# Revit family: PRD_FrankeWS_PprTwlDspnsrs_EXOSPaperTowelDispenser_EXOS637X_637B_637W
name_source: partatom
category: Specialty Equipment
revit_build: Autodesk Revit 2018 (Build: 20190510_1515(x64)
units: mm (PartAtom-declared; Revit-internal decimal feet)

## family parameters
Cut with Voids When Loaded = No
Host = Face
OmniClass Number = 23.40.20.21.17
OmniClass Title = Paper Towel Dispensers, Disposal Units
Part Type = Normal
Room Calculation Point = No
Round Connector Dimension = Use Diameter
Shared = No

## types (3) — shared parameters
AssetType = Fixed
Category = Pr_40_70_22_62, Paper Towel Dispensers
Default Elevation = 1200 mm
DispenserMaterial = PRD_AR_StainlessSteel_SatinFinished
DurationUnit = year
Features = stainless steel, surface satin finished
FillingQuantity = 1
FillingQuantityUom = Rolls
Finish = satin finished
IfcExportAs = IfcFurnitureType
IfcExportType = USERDEFINED
IntegralAccessories = incl. mounting materials
IsBuiltIn = TRUE
Lock = Key-lock
MainColor = stainless steel
Manufacturer = KWC Group AG
ManufacturerName = KWC Group AG
ManufacturerURL = www.kwc.com
Material = stainless steel
MaterialCode = 1.4301
MaterialThickness = 1.20 mm
MaximumDepthDiameterOfConsumable = 200.00 mm
MaximumWidthOfConsumable = 205.00 mm
NBSDescription = Paper towel dispensers
NBSReference = 45-35-72/344
NominalDepth = 210 mm  [stored 0.688976 ft]
NominalHeight = 425 mm  [stored 1.39436 ft]
NominalWidth = 300 mm  [stored 0.984252 ft]
ProductInformation = https://pim.kwc.com
Size = 300 x 425 x 210 mm
Style = Dispenser
SurfaceTreatment = InoxPlus (anti fingerprint)
TypeOfConsumable = Paper roll
TypeOfFixing = Screw
TypeOfMounting = Wall mounting
TypeOfOperation = Manual operation
URL = www.kwc.com
Uniclass2015Code = Pr_40_70_22_62
Uniclass2015Title = Paper towel dispensers
Uniclass2015Version = Products v1.17
Version = 1
WarrantyDurationUnit = year

## per-type parameters (varying)
| type | AdditionalPanel | BIMObjectName | Description | GrossWeight | ModelNumber | Name | NetWeight | PanelMaterial |
| EXOS637X | No | PRD_AR_PaperTowelDispensers_EXOSPaperTowelDispenser_EXOS637X | Manual paper towel dispenser for wall mounting, stainless steel with satin finish, front and casing with InoxPlus surface refinement for the reduction of finger marks and better cleaning characteristics (easy to clean), material thickness 1.2 mm, maximum roll width 205 mm, maximum roll diameter 200 mm, paper perforation length 260 mm, adjustable paper roll holder for optimised paper dispensing, includes mounting materials. | 9.64 kg | 2030022950 | Paper Towel Dispenser EXOS637X | 8.24 kg | PRD_AR_StainlessSteel_SatinFinished |
| EXOS637B | Yes | PRD_AR_PaperTowelDispensers_EXOSPaperTowelDispenser_EXOS637B | Manual paper towel dispenser for wall mounting, stainless steel with satin finish, black safety glass front panel, casing with InoxPlus surface refinement for the reduction of finger marks and better cleaning characteristics (easy to clean), material thickness 1.2 mm, maximum roll width 205 mm, maximum roll diameter 200 mm, paper perforation length 260 mm, adjustable paper roll holder for optimised paper dispensing, includes mounting materials. | 10.80 kg | 2030022951 | Paper Towel Dispenser EXOS637B | 9.37 kg | PRD_AR_Glass_Black |
| EXOS637W | Yes | PRD_AR_PaperTowelDispensers_EXOSPaperTowelDispenser_EXOS637W | Manual paper towel dispenser for wall mounting, stainless steel with satin finish, white safety glass front panel, casing with InoxPlus surface refinement for the reduction of finger marks and better cleaning characteristics (easy to clean), material thickness 1.2 mm, maximum roll width 205 mm, maximum roll diameter 200 mm, paper perforation length 260 mm, adjustable paper roll holder for optimised paper dispensing, includes mounting materials. | 10.37 kg | 2030025233 | Paper Towel Dispenser EXOS637W | 8.88 kg | PRD_AR_Glass_White |

note: column(s) folded — value = type name in every type: Model, ModelReference

note: [stored X ft] marks values corroborated as IEEE doubles in the binary element streams (Revit-internal decimal feet)

## geometry (parser evidence)
native form markers: Sweep x6
no freeform markers — native parametric forms only
